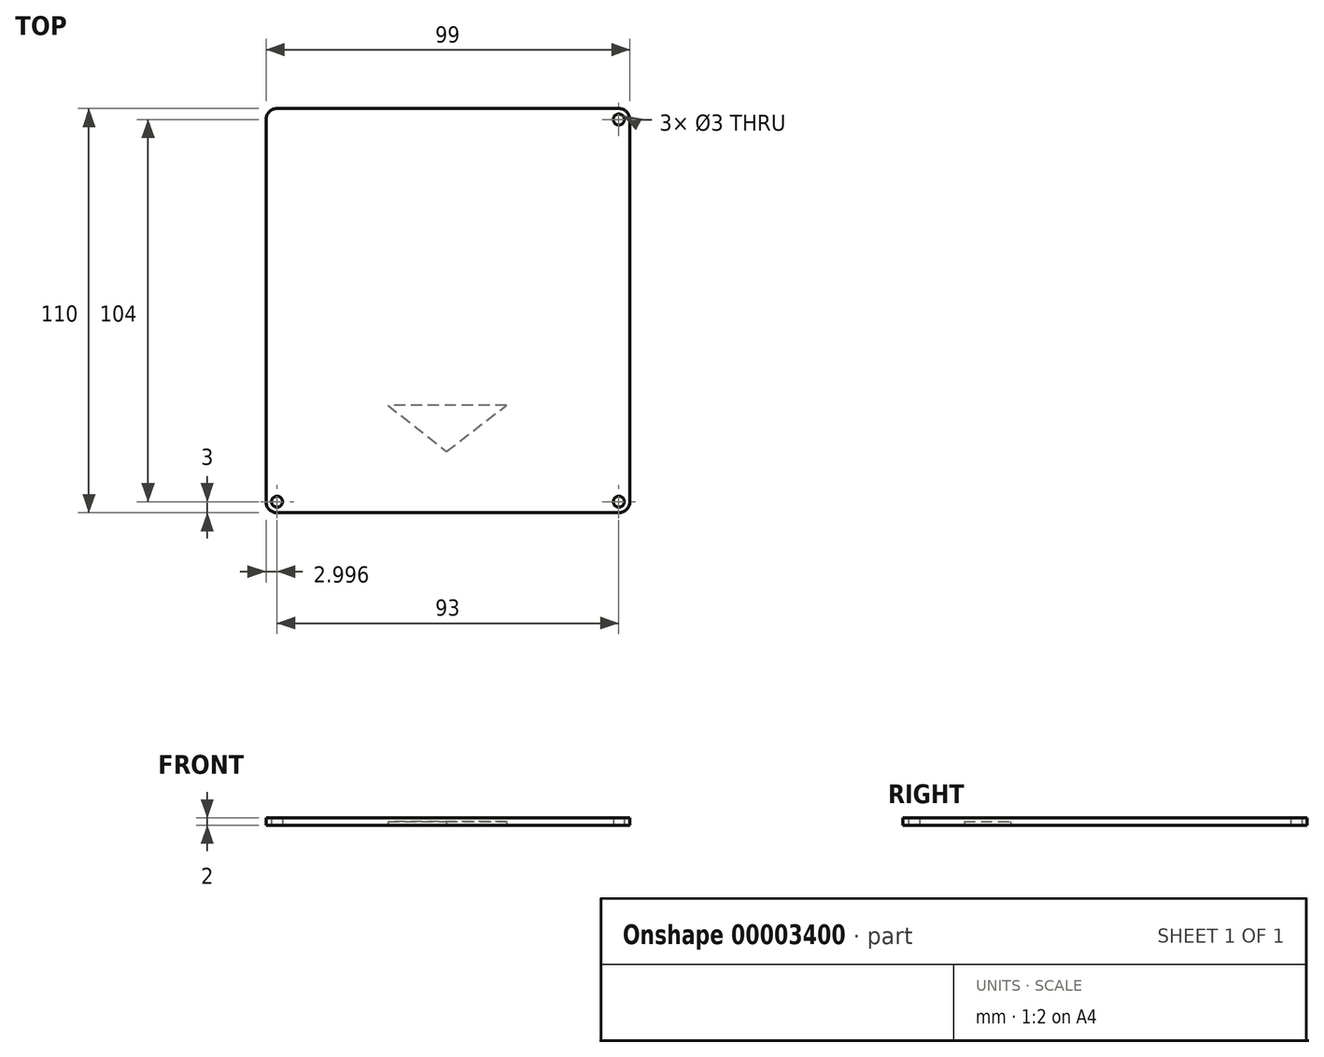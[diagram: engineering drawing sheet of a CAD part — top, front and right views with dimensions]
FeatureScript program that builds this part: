
annotation { "Feature Type Name" : "Feature", "Feature Type Description" : "" }
export const myFeature = defineFeature(function(context is Context, id is Id, definition is map)
    precondition{}
    {
        {
            var Q0;
            Q0=qCreatedBy(makeId("Top.planeOp"),FACE);
            var sketch = newSketch(context, id + "F0", { "sketchPlane" : qUnion([Q0])});
            skLineSegment(sketch, "E0.bottom", {"start": v(-82.66, 8) * mm, "end": v(16.34, 8) * mm});
            skLineSegment(sketch, "E0.top", {"start": v(-82.66, -102) * mm, "end": v(16.34, -102) * mm});
            skLineSegment(sketch, "E0.left", {"start": v(-82.66, 8) * mm, "end": v(-82.66, -102) * mm});
            skLineSegment(sketch, "E0.right", {"start": v(16.34, 8) * mm, "end": v(16.34, -102) * mm});
            skLineSegment(sketch, "E1", {"start": v(-33.16, -102) * mm, "end": v(-33.16, 8) * mm, "construction": true});
            skLineSegment(sketch, "E2", {"start": v(-82.66, -47) * mm, "end": v(16.34, -47) * mm, "construction": true});
            skCircle(sketch, "E3.0.MirrorC", {"center": v(13.34, 5) * mm, "radius": 1.5 * mm});
            skCircle(sketch, "E4.1.MirrorC", {"center": v(-79.66, -99) * mm, "radius": 1.5 * mm});
            skCircle(sketch, "E5.1.MirrorC", {"center": v(13.34, -99) * mm, "radius": 1.5 * mm});
            skSolve(sketch);
        }
        {
            var Q0;
            Q0=makeQuery(id+"F0.imprint","IMPRINT",FACE,{"disambiguationData":[TD([[makeQuery(id+"F0.imprint","IMPRINT",EDGE,{"derivedFrom":sQuery(id+"F0.wireOp",EDGE,"E0.bottom")}),-1.0]])]});
            extrude(context, id + "F1", {"entities" : qUnion([Q0]), "depth" : 2 * mm});
        }
        {
            var Q0;
            Q0=makeQuery(id+"F1.opExtrude","SWEPT_EDGE",EDGE,{"disambiguationData":[OSD([sQuery(id+"F0.wireOp",EDGE,"E0.bottom"),sQuery(id+"F0.wireOp",EDGE,"E0.left")])]});
            var Q1;
            Q1=makeQuery(id+"F1.opExtrude","SWEPT_EDGE",EDGE,{"disambiguationData":[OSD([sQuery(id+"F0.wireOp",EDGE,"E0.bottom"),sQuery(id+"F0.wireOp",EDGE,"E0.right")])]});
            var Q2;
            Q2=makeQuery(id+"F1.opExtrude","SWEPT_EDGE",EDGE,{"disambiguationData":[OSD([sQuery(id+"F0.wireOp",EDGE,"E0.top"),sQuery(id+"F0.wireOp",EDGE,"E0.right")])]});
            var Q3;
            Q3=makeQuery(id+"F1.opExtrude","SWEPT_EDGE",EDGE,{"disambiguationData":[OSD([sQuery(id+"F0.wireOp",EDGE,"E0.top"),sQuery(id+"F0.wireOp",EDGE,"E0.left")])]});
            fillet(context, id + "F2", {"entities" : qUnion([Q0, Q1, Q2, Q3]), "radius" : 3 * mm, "tangentPropagation" : true, "allowEdgeOverflow" : false});
        }
        {
            var Q0;
            Q0=makeQuery(id+"F0.imprint","IMPRINT",FACE,{"disambiguationData":[TD([[makeQuery(id+"F0.imprint","IMPRINT",EDGE,{"derivedFrom":sQuery(id+"F0.wireOp",EDGE,"E0.bottom")}),-1.0]])]});
            var sketch = newSketch(context, id + "F3", { "sketchPlane" : qUnion([Q0])});
            skLineSegment(sketch, "E6", {"start": v(-17.2, -72.74) * mm, "end": v(-49.46, -72.74) * mm});
            skLineSegment(sketch, "E7", {"start": v(-49.46, -72.74) * mm, "end": v(-33.54, -85.32) * mm});
            skLineSegment(sketch, "E8", {"start": v(-33.54, -85.32) * mm, "end": v(-17.2, -72.74) * mm});
            skSolve(sketch);
        }
        {
            var Q0;
            Q0=makeQuery(id+"F3.imprint","IMPRINT",FACE,{"disambiguationData":[TD([[makeQuery(id+"F3.imprint","IMPRINT",EDGE,{"derivedFrom":sQuery(id+"F3.wireOp",EDGE,"E6")}),1.0]])]});
            extrude(context, id + "F4", {"entities" : qUnion([Q0]), "operationType" : NewBodyOperationType.REMOVE, "depth" : 1 * mm});
        }
    });
